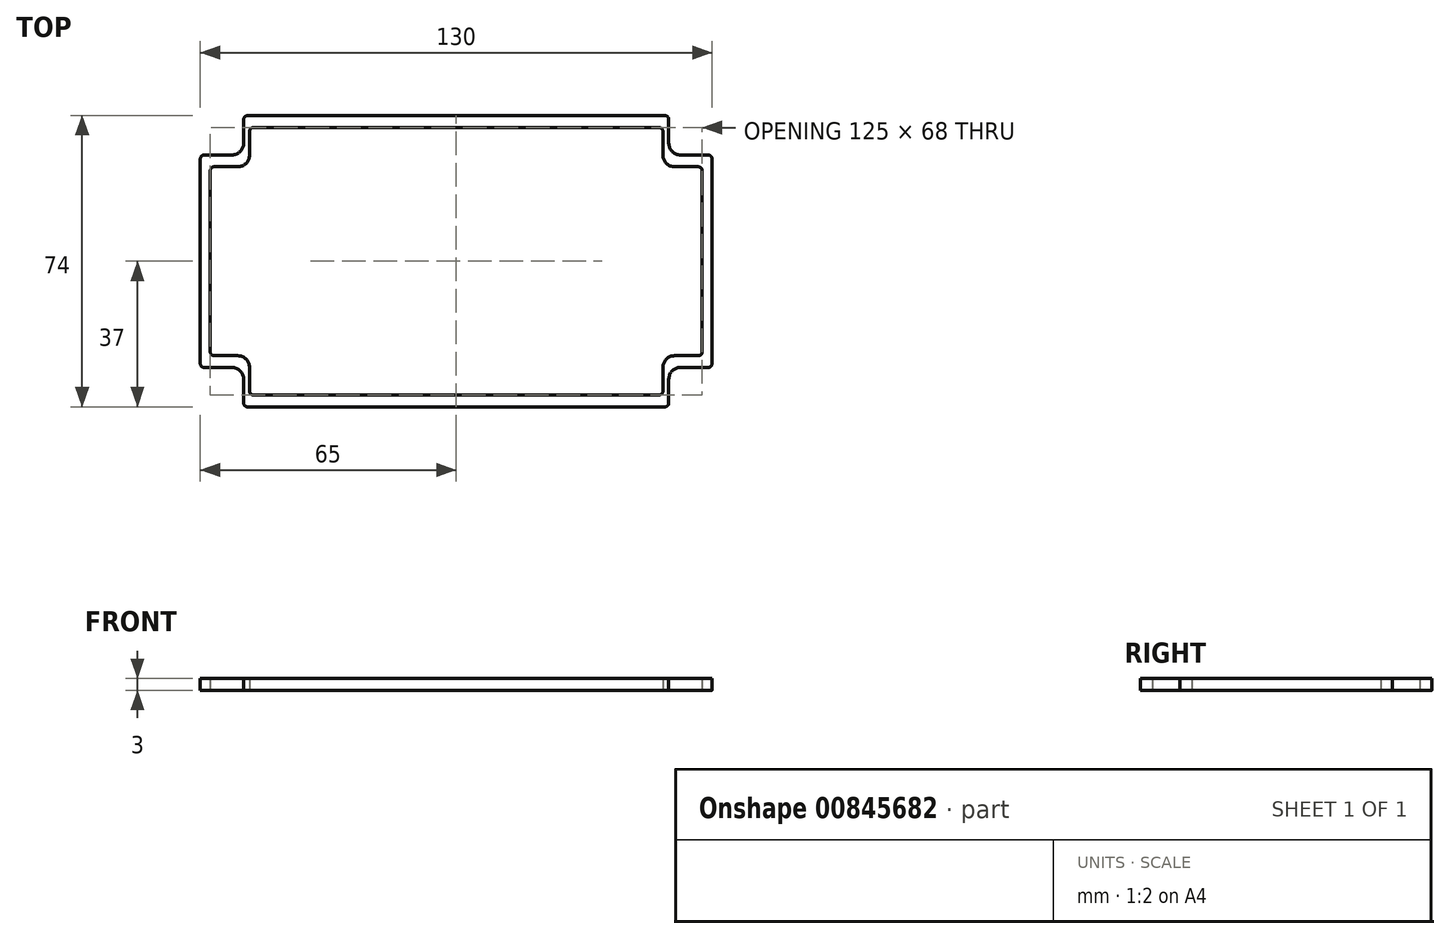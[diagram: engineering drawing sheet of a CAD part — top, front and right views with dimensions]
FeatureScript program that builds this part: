
annotation { "Feature Type Name" : "Feature", "Feature Type Description" : "" }
export const myFeature = defineFeature(function(context is Context, id is Id, definition is map)
    precondition{}
    {
        {
            var Q0;
            Q0=qCreatedBy(makeId("Top.planeOp"),FACE);
            var sketch = newSketch(context, id + "F0", { "sketchPlane" : qUnion([Q0])});
            skLineSegment(sketch, "E0.bottom", {"start": v(-53, 37) * mm, "end": v(53, 37) * mm});
            skLineSegment(sketch, "E0.top", {"start": v(-53, -37) * mm, "end": v(53, -37) * mm});
            skLineSegment(sketch, "E0.left", {"start": v(-65, 26) * mm, "end": v(-65, -26) * mm});
            skLineSegment(sketch, "E0.right", {"start": v(65, 26) * mm, "end": v(65, -26) * mm});
            skLineSegment(sketch, "E1.top", {"start": v(-64, 27) * mm, "end": v(-57, 27) * mm});
            skLineSegment(sketch, "E1.right", {"start": v(-54, 36) * mm, "end": v(-54, 30) * mm});
            skLineSegment(sketch, "E2", {"start": v(0, 17.15) * mm, "end": v(0, -17.33) * mm, "construction": true});
            skLineSegment(sketch, "E3", {"start": v(-15.24, 0) * mm, "end": v(23.95, 0) * mm, "construction": true});
            skLineSegment(sketch, "E4.MirrorCS", {"start": v(-64, -27) * mm, "end": v(-57, -27) * mm});
            skLineSegment(sketch, "E5.MirrorCS", {"start": v(-54, -36) * mm, "end": v(-54, -30) * mm});
            skLineSegment(sketch, "E6.MirrorCS", {"start": v(54, -36) * mm, "end": v(54, -30) * mm});
            skLineSegment(sketch, "E7.MirrorCS", {"start": v(64, -27) * mm, "end": v(57, -27) * mm});
            skLineSegment(sketch, "E8.MirrorCS", {"start": v(64, 27) * mm, "end": v(57, 27) * mm});
            skLineSegment(sketch, "E9.MirrorCS", {"start": v(54, 36) * mm, "end": v(54, 30) * mm});
            skPoint(sketch, "E10", {"position": v(0, 0) * mm});
            skPoint(sketch, "E11.visualSharp", {"position": v(-54, 27) * mm});
            skArc(sketch, "E11.filletArc", {"start": v(-57, 27) * mm, "mid": v(-54.88, 27.88) * mm, "end": v(-54, 30) * mm});
            skPoint(sketch, "E12.visualSharp", {"position": v(-54, -27) * mm});
            skArc(sketch, "E12.filletArc", {"start": v(-54, -30) * mm, "mid": v(-54.88, -27.88) * mm, "end": v(-57, -27) * mm});
            skPoint(sketch, "E13.visualSharp", {"position": v(54, -27) * mm});
            skArc(sketch, "E13.filletArc", {"start": v(57, -27) * mm, "mid": v(54.88, -27.88) * mm, "end": v(54, -30) * mm});
            skPoint(sketch, "E14.visualSharp", {"position": v(54, 27) * mm});
            skArc(sketch, "E14.filletArc", {"start": v(54, 30) * mm, "mid": v(54.88, 27.88) * mm, "end": v(57, 27) * mm});
            skPoint(sketch, "E15.visualSharp", {"position": v(-54, 37) * mm});
            skArc(sketch, "E15.filletArc", {"start": v(-53, 37) * mm, "mid": v(-53.7, 36.7) * mm, "end": v(-54, 36) * mm});
            skPoint(sketch, "E16.visualSharp", {"position": v(-65, 27) * mm});
            skArc(sketch, "E16.filletArc", {"start": v(-64, 27) * mm, "mid": v(-64.7, 26.7) * mm, "end": v(-65, 26) * mm});
            skPoint(sketch, "E17.visualSharp", {"position": v(-65, -27) * mm});
            skArc(sketch, "E17.filletArc", {"start": v(-65, -26) * mm, "mid": v(-64.7, -26.7) * mm, "end": v(-64, -27) * mm});
            skPoint(sketch, "E18.visualSharp", {"position": v(-54, -37) * mm});
            skArc(sketch, "E18.filletArc", {"start": v(-54, -36) * mm, "mid": v(-53.7, -36.7) * mm, "end": v(-53, -37) * mm});
            skPoint(sketch, "E19.visualSharp", {"position": v(54, -37) * mm});
            skArc(sketch, "E19.filletArc", {"start": v(53, -37) * mm, "mid": v(53.7, -36.7) * mm, "end": v(54, -36) * mm});
            skPoint(sketch, "E20.visualSharp", {"position": v(65, -27) * mm});
            skArc(sketch, "E20.filletArc", {"start": v(64, -27) * mm, "mid": v(64.7, -26.7) * mm, "end": v(65, -26) * mm});
            skPoint(sketch, "E21.visualSharp", {"position": v(65, 27) * mm});
            skArc(sketch, "E21.filletArc", {"start": v(65, 26) * mm, "mid": v(64.7, 26.7) * mm, "end": v(64, 27) * mm});
            skPoint(sketch, "E22.visualSharp", {"position": v(54, 37) * mm});
            skArc(sketch, "E22.filletArc", {"start": v(54, 36) * mm, "mid": v(53.7, 36.7) * mm, "end": v(53, 37) * mm});
            skLineSegment(sketch, "E23.bottom", {"start": v(-51.5, 34) * mm, "end": v(51.5, 34) * mm});
            skLineSegment(sketch, "E23.top", {"start": v(-51.5, -34) * mm, "end": v(51.5, -34) * mm});
            skLineSegment(sketch, "E23.left", {"start": v(-62.5, 23) * mm, "end": v(-62.5, -23) * mm});
            skLineSegment(sketch, "E23.right", {"start": v(62.5, 23) * mm, "end": v(62.5, -23) * mm});
            skLineSegment(sketch, "E24.top", {"start": v(61.5, 24) * mm, "end": v(55.5, 24) * mm});
            skLineSegment(sketch, "E24.right", {"start": v(52.5, 33) * mm, "end": v(52.5, 27) * mm});
            skLineSegment(sketch, "E25.MirrorCS", {"start": v(-52.5, 33) * mm, "end": v(-52.5, 27) * mm});
            skLineSegment(sketch, "E26.MirrorCS", {"start": v(-61.5, 24) * mm, "end": v(-55.5, 24) * mm});
            skLineSegment(sketch, "E27.MirrorCS", {"start": v(-61.5, -24) * mm, "end": v(-55.5, -24) * mm});
            skLineSegment(sketch, "E28.MirrorCS", {"start": v(-52.5, -33) * mm, "end": v(-52.5, -27) * mm});
            skLineSegment(sketch, "E29.MirrorCS", {"start": v(52.5, -33) * mm, "end": v(52.5, -27) * mm});
            skLineSegment(sketch, "E30.MirrorCS", {"start": v(61.5, -24) * mm, "end": v(55.5, -24) * mm});
            skPoint(sketch, "E31.orphan", {"position": v(-62.5, -34) * mm});
            skPoint(sketch, "E32.visualSharp", {"position": v(-52.5, 24) * mm});
            skArc(sketch, "E32.filletArc", {"start": v(-55.5, 24) * mm, "mid": v(-53.38, 24.88) * mm, "end": v(-52.5, 27) * mm});
            skPoint(sketch, "E33.visualSharp", {"position": v(-52.5, -24) * mm});
            skArc(sketch, "E33.filletArc", {"start": v(-52.5, -27) * mm, "mid": v(-53.38, -24.88) * mm, "end": v(-55.5, -24) * mm});
            skPoint(sketch, "E34.visualSharp", {"position": v(52.5, 24) * mm});
            skArc(sketch, "E34.filletArc", {"start": v(52.5, 27) * mm, "mid": v(53.38, 24.88) * mm, "end": v(55.5, 24) * mm});
            skPoint(sketch, "E35.visualSharp", {"position": v(52.5, -24) * mm});
            skArc(sketch, "E35.filletArc", {"start": v(55.5, -24) * mm, "mid": v(53.38, -24.88) * mm, "end": v(52.5, -27) * mm});
            skPoint(sketch, "E36.visualSharp", {"position": v(-62.5, 24) * mm});
            skArc(sketch, "E36.filletArc", {"start": v(-61.5, 24) * mm, "mid": v(-62.2, 23.7) * mm, "end": v(-62.5, 23) * mm});
            skPoint(sketch, "E37.visualSharp", {"position": v(-52.5, 34) * mm});
            skArc(sketch, "E37.filletArc", {"start": v(-51.5, 34) * mm, "mid": v(-52.2, 33.7) * mm, "end": v(-52.5, 33) * mm});
            skPoint(sketch, "E38.visualSharp", {"position": v(52.5, 34) * mm});
            skArc(sketch, "E38.filletArc", {"start": v(52.5, 33) * mm, "mid": v(52.2, 33.7) * mm, "end": v(51.5, 34) * mm});
            skPoint(sketch, "E39.visualSharp", {"position": v(62.5, 24) * mm});
            skArc(sketch, "E39.filletArc", {"start": v(62.5, 23) * mm, "mid": v(62.2, 23.7) * mm, "end": v(61.5, 24) * mm});
            skPoint(sketch, "E40.visualSharp", {"position": v(62.5, -24) * mm});
            skArc(sketch, "E40.filletArc", {"start": v(61.5, -24) * mm, "mid": v(62.2, -23.7) * mm, "end": v(62.5, -23) * mm});
            skPoint(sketch, "E41.visualSharp", {"position": v(52.5, -34) * mm});
            skArc(sketch, "E41.filletArc", {"start": v(51.5, -34) * mm, "mid": v(52.2, -33.7) * mm, "end": v(52.5, -33) * mm});
            skPoint(sketch, "E42.visualSharp", {"position": v(-52.5, -34) * mm});
            skArc(sketch, "E42.filletArc", {"start": v(-52.5, -33) * mm, "mid": v(-52.2, -33.7) * mm, "end": v(-51.5, -34) * mm});
            skPoint(sketch, "E43.visualSharp", {"position": v(-62.5, -24) * mm});
            skArc(sketch, "E43.filletArc", {"start": v(-62.5, -23) * mm, "mid": v(-62.2, -23.7) * mm, "end": v(-61.5, -24) * mm});
            skSolve(sketch);
        }
        {
            var Q0;
            Q0 = qSketchRegion(id + "F0", true);
            extrude(context, id + "F1", {"entities" : qUnion([Q0]), "depth" : 3 * mm, "offsetDistance" : 25 * mm});
        }
    });
